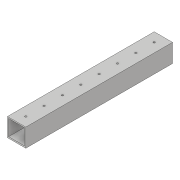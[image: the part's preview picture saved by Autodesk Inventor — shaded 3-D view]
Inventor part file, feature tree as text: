
AUTODESK INVENTOR PART (.ipt)
format: ipt  version: 2018 (Build 220112000, 112)  size: 105,984 bytes
history: native  units: in
note: dims shown in document units (in); Inventor stores cm internally (conversion verified against a paired STEP export)
features: sketch x2, extrude x1, hole x1
ambient origin geometry x8: Origin, YZ Plane, XZ Plane, XY Plane, X Axis, Y Axis, Z Axis, Center Point
bodies: Solid1 (feature_tree)
feature tree (4):
  extrude  "Extrusion1"  Depth=1.0in
  hole  "Hole1"  [1 undecoded]
  sketch  "Sketch1"  dims[d0=1.0in d1=1.0in]
  sketch  "Sketch2"  dims[d2=0.0625in d3=0.0625in d4=8.0in d5=0.0in d6=0.5in d7=0.5in d8=5.9055in d10=1.0in d11=0.3937in d13=1.0in d15=0.1in d16=0.75in d17=0.375in d18=0.25in d19=0.5635in d20=1.0in d21=0.8108in]
note: 1 required parameter value undecoded (feature->parameter linkage not recoverable at this tier; creation-order binding heuristic only, values carry confidence <= 0.55)
